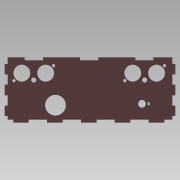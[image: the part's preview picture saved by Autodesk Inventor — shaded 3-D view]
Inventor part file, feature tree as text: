
AUTODESK INVENTOR PART (.ipt)
format: ipt  version: 2015 SP1 (Build 190203100, 203)  size: 190,976 bytes
history: native  units: mm
features: extrude x1, sketch x1
ambient origin geometry x8: Origin, YZ Plane, XZ Plane, XY Plane, X Axis, Y Axis, Z Axis, Center Point
bodies: Solid1 (feature_tree)
feature tree (2):
  extrude  "Extrusion1"  Depth=15.0mm
  sketch  "Sketch1"  dims[d2=20.0mm d4=15.0mm d5=3.0mm d8=30.0mm d10=32.5mm d11=30.0mm d13=32.5mm d16=1.5mm d17=3.0mm d18=10.0mm d19=20.0mm d21=20.0mm d22=20.0mm d24=20.0mm d27=3.0mm d28=0.0mm]
